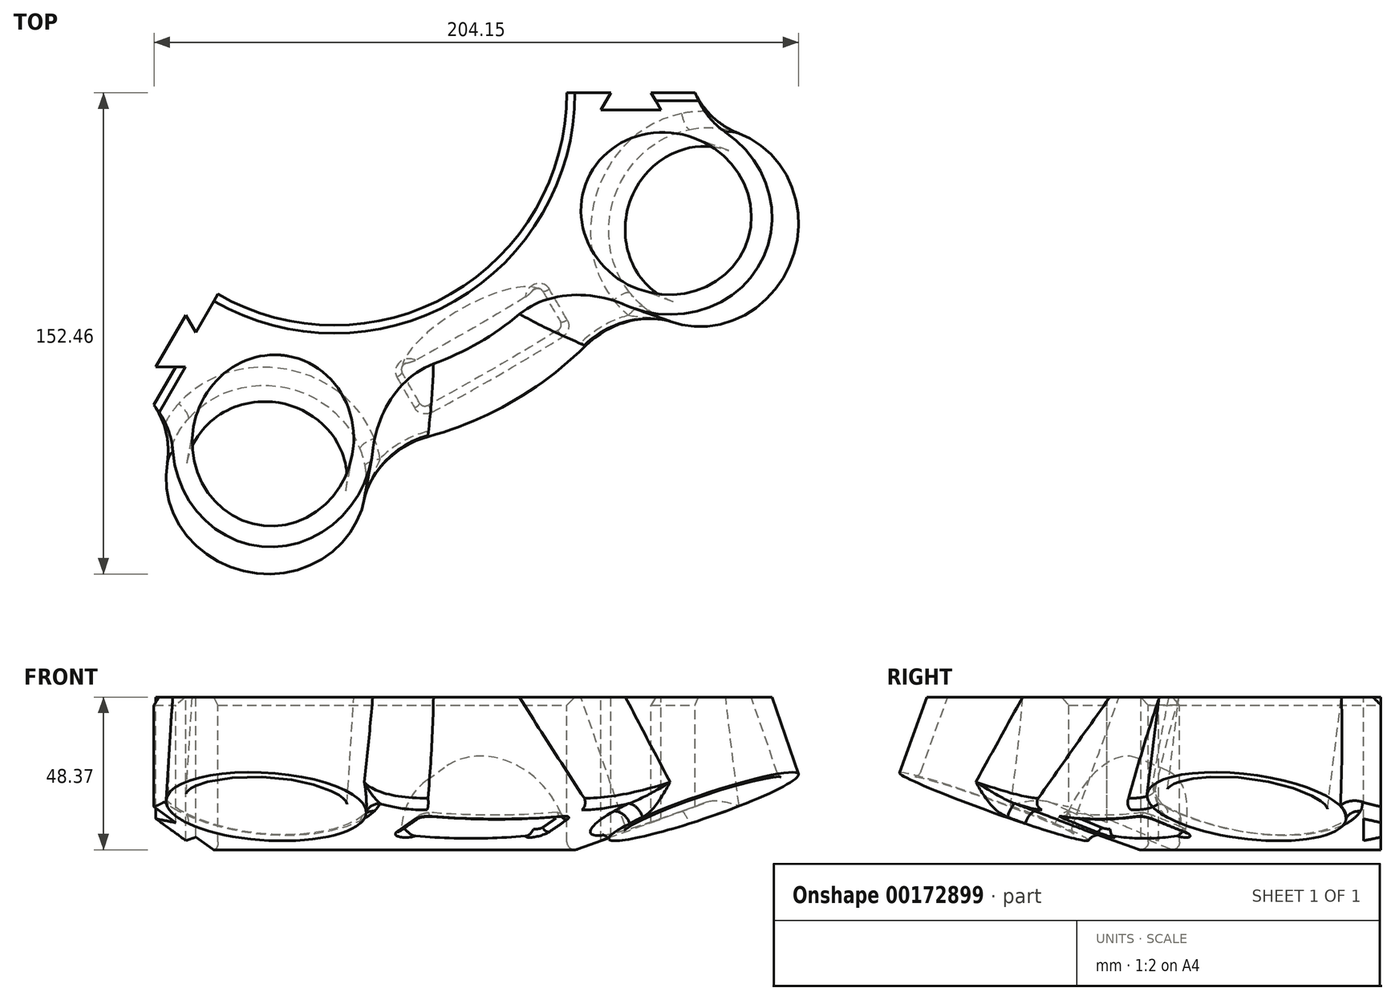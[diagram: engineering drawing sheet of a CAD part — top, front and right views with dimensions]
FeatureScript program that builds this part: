
annotation { "Feature Type Name" : "Feature", "Feature Type Description" : "" }
export const myFeature = defineFeature(function(context is Context, id is Id, definition is map)
    precondition{}
    {
        {
            var Q0;
            Q0=qCreatedBy(makeId("Top.planeOp"),FACE);
            var sketch = newSketch(context, id + "F0", { "sketchPlane" : qUnion([Q0])});
            skArc(sketch, "E0", {"start": v(36.2, 62.7) * mm, "mid": v(-36.2, 62.7) * mm, "end": v(-72.39, 0) * mm});
            skArc(sketch, "E1", {"start": v(55.44, 96.02) * mm, "mid": v(43.6, 101.94) * mm, "end": v(31.13, 106.41) * mm});
            skLineSegment(sketch, "E2", {"start": v(-72.4, 0) * mm, "end": v(-110.87, 0) * mm});
            skLineSegment(sketch, "E3", {"start": v(36.2, 62.7) * mm, "end": v(55.44, 96.02) * mm});
            skLineSegment(sketch, "E4", {"start": v(-22.63, 115.53) * mm, "end": v(0, 0) * mm, "construction": true});
            skLineSegment(sketch, "E5", {"start": v(-90.19, 75.67) * mm, "end": v(0, 0) * mm, "construction": true});
            skPoint(sketch, "E6.visualSharp", {"position": v(-104.04, 38.3) * mm});
            skPoint(sketch, "E7.visualSharp", {"position": v(-57.88, 98.1) * mm});
            skPoint(sketch, "E8.visualSharp", {"position": v(16.78, 109.6) * mm});
            skArc(sketch, "E9.converted", {"start": v(55.44, 96.02) * mm, "mid": v(-55.44, 96.02) * mm, "end": v(-110.87, 0) * mm});
            skSolve(sketch);
        }
        {
            var Q0;
            Q0=qCreatedBy(makeId("Front.planeOp"),FACE);
            var Q1;
            Q1=sQuery(id+"F0.wireOp",EDGE,"E5");
            cPlane(context, id + "F1", {"entities" : qUnion([Q0, Q1]), "cplaneType" : CPlaneType.LINE_ANGLE, "offset" : 25.4 * mm, "angle" : 0 * degree, "width" : 152.4 * mm, "height" : 152.4 * mm});
        }
        {
            var Q0;
            Q0=qCreatedBy(id+"F1.planeOp",FACE);
            var sketch = newSketch(context, id + "F2", { "sketchPlane" : qUnion([Q0])});
            skLineSegment(sketch, "E10", {"start": v(91.59, 0) * mm, "end": v(119.1, 10.02) * mm, "construction": true});
            skSolve(sketch);
        }
        {
            var Q0;
            Q0=qCreatedBy(id+"F1.planeOp",FACE);
            var Q1;
            Q1=sQuery(id+"F0.wireOp",EDGE,"E4");
            cPlane(context, id + "F3", {"entities" : qUnion([Q0, Q1]), "cplaneType" : CPlaneType.LINE_ANGLE, "offset" : 25.4 * mm, "angle" : 0 * degree, "width" : 152.4 * mm, "height" : 152.4 * mm});
        }
        {
            var Q0;
            Q0=qCreatedBy(id+"F3.planeOp",FACE);
            var sketch = newSketch(context, id + "F4", { "sketchPlane" : qUnion([Q0])});
            skLineSegment(sketch, "E11", {"start": v(-91.91, 0) * mm, "end": v(-139.27, 17.24) * mm, "construction": true});
            skSolve(sketch);
        }
        {
            var Q0;
            Q0=qCreatedBy(id+"F1.planeOp",FACE);
            var sketch = newSketch(context, id + "F5", { "sketchPlane" : qUnion([Q0])});
            skLineSegment(sketch, "E12", {"start": v(0, 0) * mm, "end": v(124.46, 0) * mm, "construction": true});
            skLineSegment(sketch, "E13", {"start": v(0, 53.66) * mm, "end": v(0, 0) * mm, "construction": true});
            skLineSegment(sketch, "E14", {"start": v(124.46, 0) * mm, "end": v(106, 50.72) * mm, "construction": true});
            skLineSegment(sketch, "E15", {"start": v(148.36, 8.7) * mm, "end": v(154.3, 10.86) * mm});
            skLineSegment(sketch, "E16", {"start": v(154.3, 10.86) * mm, "end": v(134.75, 64.56) * mm});
            skLineSegment(sketch, "E17", {"start": v(134.75, 64.56) * mm, "end": v(129.03, 61.8) * mm});
            skLineSegment(sketch, "E18", {"start": v(148.36, 8.7) * mm, "end": v(129.03, 61.8) * mm});
            skSolve(sketch);
        }
        {
            var Q0;
            Q0 = qSketchRegion(id + "F5", true);
            var Q1;
            Q1=sQuery(id+"F5.wireOp",EDGE,"E14");
            revolve(context, id + "F6", {"entities" : qUnion([Q0]), "axis" : qUnion([Q1]), "revolveType" : RevolveType.FULL});
        }
        {
            var Q0;
            Q0=makeQuery(id+"F6.opRevolve","SWEPT_BODY",BODY,{"disambiguationData":[OSD([sQuery(id+"F5.wireOp",EDGE,"E15"),sQuery(id+"F5.wireOp",EDGE,"E16"),sQuery(id+"F5.wireOp",EDGE,"E17"),sQuery(id+"F5.wireOp",EDGE,"E18")])]});
            var Q1;
            Q1=sQuery(id+"F5.wireOp",EDGE,"E13");
            circularPattern(context, id + "F7", {"entities" : qUnion([Q0]), "axis" : qUnion([Q1]), "angle" : 40 * degree, "instanceCount" : 2});
        }
        {
            var Q0;
            Q0=qCreatedBy(id+"F1.planeOp",FACE);
            var sketch = newSketch(context, id + "F8", { "sketchPlane" : qUnion([Q0])});
            skLineSegment(sketch, "E19", {"start": v(73.66, 34.68) * mm, "end": v(73.66, -14.78) * mm});
            skLineSegment(sketch, "E20", {"start": v(73.66, -14.78) * mm, "end": v(73.66, 34.68) * mm});
            skLineSegment(sketch, "E21", {"start": v(73.66, 34.68) * mm, "end": v(91.44, 34.68) * mm});
            skLineSegment(sketch, "E22", {"start": v(114.27, 0) * mm, "end": v(73.66, -14.78) * mm});
            skLineSegment(sketch, "E23", {"start": v(91.44, 34.68) * mm, "end": v(114.27, 0) * mm});
            skSolve(sketch);
        }
        {
            var Q0;
            Q0 = qSketchRegion(id + "F8", true);
            var Q1;
            Q1=sQuery(id+"F5.wireOp",EDGE,"E13");
            revolve(context, id + "F9", {"entities" : qUnion([Q0]), "axis" : qUnion([Q1]), "revolveType" : RevolveType.TWO_DIRECTIONS, "angle" : 80 * degree, "angleBack" : 320 * degree});
        }
        {
            var Q0;
            Q0=makeQuery(id+"F6.opRevolve","SWEPT_FACE",FACE,{"disambiguationData":[OSD([sQuery(id+"F5.wireOp",EDGE,"E15")])]});
            var sketch = newSketch(context, id + "F10", { "sketchPlane" : qUnion([Q0])});
            skCircle(sketch, "E24", {"center": v(-87.24, -77.9) * mm, "radius": 25.53 * mm});
            skSolve(sketch);
        }
        {
            var Q0;
            Q0 = qSketchRegion(id + "F10", true);
            extrude(context, id + "F11", {"entities" : qUnion([Q0]), "operationType" : NewBodyOperationType.REMOVE, "endBound" : BoundingType.THROUGH_ALL, "depth" : 25.4 * mm, "hasSecondDirection" : true, "secondDirectionBound" : BoundingType.THROUGH_ALL, "secondDirectionOppositeDirection" : true, "secondDirectionDepth" : 25.4 * mm});
        }
        {
            var Q0;
            Q0=makeQuery(id+"F7.opPattern","COPY",FACE,{"derivedFrom":makeQuery(id+"F6.opRevolve","SWEPT_FACE",FACE,{"disambiguationData":[OSD([sQuery(id+"F5.wireOp",EDGE,"E15")])]}),"instanceName":"1"});
            var sketch = newSketch(context, id + "F12", { "sketchPlane" : qUnion([Q0])});
            skCircle(sketch, "E25", {"center": v(-19.12, -115.38) * mm, "radius": 25.53 * mm});
            skSolve(sketch);
        }
        {
            var Q0;
            Q0 = qSketchRegion(id + "F12", true);
            extrude(context, id + "F13", {"entities" : qUnion([Q0]), "operationType" : NewBodyOperationType.REMOVE, "endBound" : BoundingType.THROUGH_ALL, "depth" : 25.4 * mm, "hasSecondDirection" : true, "secondDirectionBound" : BoundingType.THROUGH_ALL, "secondDirectionOppositeDirection" : true, "secondDirectionDepth" : 25.4 * mm});
        }
        {
            var Q0;
            Q0=makeQuery(id+"F9.opRevolve","CAP_FACE",FACE,{"disambiguationData":[OSD([sQuery(id+"F8.wireOp",EDGE,"E19"),sQuery(id+"F8.wireOp",EDGE,"E20"),sQuery(id+"F8.wireOp",EDGE,"E21"),sQuery(id+"F8.wireOp",EDGE,"E22"),sQuery(id+"F8.wireOp",EDGE,"E23")])],"isStart":true});
            var sketch = newSketch(context, id + "F14", { "sketchPlane" : qUnion([Q0])});
            skLineSegment(sketch, "E26", {"start": v(-73.66, 34.68) * mm, "end": v(-150.81, 34.68) * mm});
            skLineSegment(sketch, "E27", {"start": v(-150.81, 69.54) * mm, "end": v(-73.66, 69.54) * mm});
            skLineSegment(sketch, "E28", {"start": v(-150.81, 69.54) * mm, "end": v(-150.81, 34.68) * mm});
            skLineSegment(sketch, "E29", {"start": v(-73.66, 69.54) * mm, "end": v(-73.66, 34.68) * mm});
            skSolve(sketch);
        }
        {
            var Q0;
            Q0 = qSketchRegion(id + "F14", true);
            var Q1;
            Q1=sQuery(id+"F5.wireOp",EDGE,"E13");
            revolve(context, id + "F15", {"operationType" : NewBodyOperationType.REMOVE, "entities" : qUnion([Q0]), "axis" : qUnion([Q1]), "revolveType" : RevolveType.ONE_DIRECTION, "angle" : 120 * degree});
        }
        {
            var Q0;
            Q0=makeQuery(id+"F6.opRevolve","SWEPT_BODY",BODY,{"disambiguationData":[OSD([sQuery(id+"F5.wireOp",EDGE,"E15"),sQuery(id+"F5.wireOp",EDGE,"E16"),sQuery(id+"F5.wireOp",EDGE,"E17"),sQuery(id+"F5.wireOp",EDGE,"E18")])]});
            var Q1;
            Q1=makeQuery(id+"F7.opPattern","COPY",BODY,{"derivedFrom":makeQuery(id+"F6.opRevolve","SWEPT_BODY",BODY,{"disambiguationData":[OSD([sQuery(id+"F5.wireOp",EDGE,"E15"),sQuery(id+"F5.wireOp",EDGE,"E16"),sQuery(id+"F5.wireOp",EDGE,"E17"),sQuery(id+"F5.wireOp",EDGE,"E18")])]}),"instanceName":"1"});
            var Q2;
            Q2=makeQuery(id+"F9.opRevolve","SWEPT_BODY",BODY,{"disambiguationData":[OSD([sQuery(id+"F8.wireOp",EDGE,"E19"),sQuery(id+"F8.wireOp",EDGE,"E20"),sQuery(id+"F8.wireOp",EDGE,"E21"),sQuery(id+"F8.wireOp",EDGE,"E22"),sQuery(id+"F8.wireOp",EDGE,"E23")])]});
            var Q3;
            Q3=sQuery(id+"F5.wireOp",EDGE,"E13");
            circularPattern(context, id + "F16", {"entities" : qUnion([Q0, Q1, Q2]), "axis" : qUnion([Q3]), "angle" : 120 * degree, "instanceCount" : 3});
        }
        {
            var Q0;
            Q0=qCreatedBy(makeId("Front.planeOp"),FACE);
            var sketch = newSketch(context, id + "F17", { "sketchPlane" : qUnion([Q0])});
            skLineSegment(sketch, "E30", {"start": v(-105.19, -47.93) * mm, "end": v(-151.02, -47.93) * mm, "construction": true});
            skLineSegment(sketch, "E31", {"start": v(-102.98, -8.48) * mm, "end": v(-100.37, -1.32) * mm});
            skLineSegment(sketch, "E32", {"start": v(-102.98, -8.48) * mm, "end": v(-129.23, 1.07) * mm});
            skLineSegment(sketch, "E33", {"start": v(-129.23, 1.07) * mm, "end": v(-126.63, 8.23) * mm});
            skLineSegment(sketch, "E34", {"start": v(-126.63, 8.23) * mm, "end": v(-100.37, -1.32) * mm});
            skLineSegment(sketch, "E35", {"start": v(-135.33, -8.25) * mm, "end": v(-127.68, 12.78) * mm, "construction": true});
            skSolve(sketch);
        }
        {
            var Q0;
            Q0=makeQuery(id+"FokKAQGzDr6NISq_2.opRevolve","SWEPT_BODY",BODY,{"disambiguationData":[OSD([sQuery(id+"F17.wireOp",EDGE,"E31"),sQuery(id+"F17.wireOp",EDGE,"E32"),sQuery(id+"F17.wireOp",EDGE,"E33"),sQuery(id+"F17.wireOp",EDGE,"E34")])]});
            var Q1;
            Q1=makeQuery(id+"F9.opRevolve","SWEPT_BODY",BODY,{"disambiguationData":[OSD([sQuery(id+"F8.wireOp",EDGE,"E19"),sQuery(id+"F8.wireOp",EDGE,"E20"),sQuery(id+"F8.wireOp",EDGE,"E21"),sQuery(id+"F8.wireOp",EDGE,"E22"),sQuery(id+"F8.wireOp",EDGE,"E23")])]});
            var Q2;
            Q2=sQuery(id+"F5.wireOp",EDGE,"E13");
            circularPattern(context, id + "F18", {"entities" : qUnion([Q0, Q1]), "axis" : qUnion([Q2]), "angle" : 120 * degree, "instanceCount" : 3});
        }
        {
            var Q0;
            {var subQ0=sQuery(id+"F8.wireOp",EDGE,"E22");var subQ2=sQuery(id+"F8.wireOp",EDGE,"E23");var subQ4=sQuery(id+"F8.wireOp",EDGE,"E21");var subQ5=makeQuery(id+"F11.opExtrude","SWEPT_FACE",FACE,{"disambiguationData":[OSD([sQuery(id+"F10.wireOp",EDGE,"E24")])]});Q0=makeQuery(id+"F16.opPattern","COPY",EDGE,{"derivedFrom":makeQuery(id+"F13.boolean.opBoolean","SPLIT",EDGE,{"disambiguationData":[TD([makeQuery(id+"F11.boolean.opBoolean","COPY",FACE,{"disambiguationData":[TD([makeQuery(id+"F9.opRevolve","SWEPT_FACE",FACE,{"disambiguationData":[OSD([subQ4])]})])],"derivedFrom":subQ5})])],"derivedFrom":makeQuery(id+"F11.boolean.opBoolean","SPLIT",EDGE,{"disambiguationData":[TD([makeQuery(id+"F9.opRevolve","CAP_FACE",FACE,{"disambiguationData":[OSD([sQuery(id+"F8.wireOp",EDGE,"E19"),sQuery(id+"F8.wireOp",EDGE,"E20"),subQ4,subQ0,subQ2])],"isStart":false})])],"derivedFrom":makeQuery(id+"F9.opRevolve","SWEPT_EDGE",EDGE,{"disambiguationData":[OSD([subQ0,subQ2])]})})}),"instanceName":"1"});}
            fillet(context, id + "F19", {"entities" : qUnion([Q0]), "radius" : 5.08 * mm, "tangentPropagation" : true, "allowEdgeOverflow" : false});
        }
        {
            var Q0;
            Q0=makeQuery(id+"F18.opPattern","COPY",BODY,{"derivedFrom":makeQuery(id+"FokKAQGzDr6NISq_2.opRevolve","SWEPT_BODY",BODY,{"disambiguationData":[OSD([sQuery(id+"F17.wireOp",EDGE,"E31"),sQuery(id+"F17.wireOp",EDGE,"E32"),sQuery(id+"F17.wireOp",EDGE,"E33"),sQuery(id+"F17.wireOp",EDGE,"E34")])]}),"instanceName":"1"});
            var Q1;
            Q1=makeQuery(id+"F6.opRevolve","SWEPT_BODY",BODY,{"disambiguationData":[OSD([sQuery(id+"F5.wireOp",EDGE,"E15"),sQuery(id+"F5.wireOp",EDGE,"E16"),sQuery(id+"F5.wireOp",EDGE,"E17"),sQuery(id+"F5.wireOp",EDGE,"E18")])]});
            var Q2;
            Q2=makeQuery(id+"F16.opPattern","COPY",BODY,{"derivedFrom":makeQuery(id+"F9.opRevolve","SWEPT_BODY",BODY,{"disambiguationData":[OSD([sQuery(id+"F8.wireOp",EDGE,"E19"),sQuery(id+"F8.wireOp",EDGE,"E20"),sQuery(id+"F8.wireOp",EDGE,"E21"),sQuery(id+"F8.wireOp",EDGE,"E22"),sQuery(id+"F8.wireOp",EDGE,"E23")])]}),"instanceName":"1"});
            var Q3;
            Q3=makeQuery(id+"F18.opPattern","COPY",BODY,{"derivedFrom":makeQuery(id+"F9.opRevolve","SWEPT_BODY",BODY,{"disambiguationData":[OSD([sQuery(id+"F8.wireOp",EDGE,"E19"),sQuery(id+"F8.wireOp",EDGE,"E20"),sQuery(id+"F8.wireOp",EDGE,"E21"),sQuery(id+"F8.wireOp",EDGE,"E22"),sQuery(id+"F8.wireOp",EDGE,"E23")])]}),"instanceName":"1"});
            var Q4;
            Q4=makeQuery(id+"F18.opPattern","COPY",BODY,{"derivedFrom":makeQuery(id+"F9.opRevolve","SWEPT_BODY",BODY,{"disambiguationData":[OSD([sQuery(id+"F8.wireOp",EDGE,"E19"),sQuery(id+"F8.wireOp",EDGE,"E20"),sQuery(id+"F8.wireOp",EDGE,"E21"),sQuery(id+"F8.wireOp",EDGE,"E22"),sQuery(id+"F8.wireOp",EDGE,"E23")])]}),"instanceName":"2"});
            var Q5;
            Q5=makeQuery(id+"F7.opPattern","COPY",BODY,{"derivedFrom":makeQuery(id+"F6.opRevolve","SWEPT_BODY",BODY,{"disambiguationData":[OSD([sQuery(id+"F5.wireOp",EDGE,"E15"),sQuery(id+"F5.wireOp",EDGE,"E16"),sQuery(id+"F5.wireOp",EDGE,"E17"),sQuery(id+"F5.wireOp",EDGE,"E18")])]}),"instanceName":"1"});
            var Q6;
            Q6=makeQuery(id+"F16.opPattern","COPY",BODY,{"derivedFrom":makeQuery(id+"F6.opRevolve","SWEPT_BODY",BODY,{"disambiguationData":[OSD([sQuery(id+"F5.wireOp",EDGE,"E15"),sQuery(id+"F5.wireOp",EDGE,"E16"),sQuery(id+"F5.wireOp",EDGE,"E17"),sQuery(id+"F5.wireOp",EDGE,"E18")])]}),"instanceName":"1"});
            var Q7;
            Q7=makeQuery(id+"FokKAQGzDr6NISq_2.opRevolve","SWEPT_BODY",BODY,{"disambiguationData":[OSD([sQuery(id+"F17.wireOp",EDGE,"E31"),sQuery(id+"F17.wireOp",EDGE,"E32"),sQuery(id+"F17.wireOp",EDGE,"E33"),sQuery(id+"F17.wireOp",EDGE,"E34")])]});
            var Q8;
            Q8=makeQuery(id+"F16.opPattern","COPY",BODY,{"derivedFrom":makeQuery(id+"F9.opRevolve","SWEPT_BODY",BODY,{"disambiguationData":[OSD([sQuery(id+"F8.wireOp",EDGE,"E19"),sQuery(id+"F8.wireOp",EDGE,"E20"),sQuery(id+"F8.wireOp",EDGE,"E21"),sQuery(id+"F8.wireOp",EDGE,"E22"),sQuery(id+"F8.wireOp",EDGE,"E23")])]}),"instanceName":"2"});
            var Q9;
            Q9=makeQuery(id+"F16.opPattern","COPY",BODY,{"derivedFrom":makeQuery(id+"F7.opPattern","COPY",BODY,{"derivedFrom":makeQuery(id+"F6.opRevolve","SWEPT_BODY",BODY,{"disambiguationData":[OSD([sQuery(id+"F5.wireOp",EDGE,"E15"),sQuery(id+"F5.wireOp",EDGE,"E16"),sQuery(id+"F5.wireOp",EDGE,"E17"),sQuery(id+"F5.wireOp",EDGE,"E18")])]}),"instanceName":"1"}),"instanceName":"2"});
            var Q10;
            Q10=makeQuery(id+"F18.opPattern","COPY",BODY,{"derivedFrom":makeQuery(id+"FokKAQGzDr6NISq_2.opRevolve","SWEPT_BODY",BODY,{"disambiguationData":[OSD([sQuery(id+"F17.wireOp",EDGE,"E31"),sQuery(id+"F17.wireOp",EDGE,"E32"),sQuery(id+"F17.wireOp",EDGE,"E33"),sQuery(id+"F17.wireOp",EDGE,"E34")])]}),"instanceName":"2"});
            var Q11;
            Q11=makeQuery(id+"F16.opPattern","COPY",BODY,{"derivedFrom":makeQuery(id+"F7.opPattern","COPY",BODY,{"derivedFrom":makeQuery(id+"F6.opRevolve","SWEPT_BODY",BODY,{"disambiguationData":[OSD([sQuery(id+"F5.wireOp",EDGE,"E15"),sQuery(id+"F5.wireOp",EDGE,"E16"),sQuery(id+"F5.wireOp",EDGE,"E17"),sQuery(id+"F5.wireOp",EDGE,"E18")])]}),"instanceName":"1"}),"instanceName":"1"});
            var Q12;
            Q12=makeQuery(id+"F16.opPattern","COPY",BODY,{"derivedFrom":makeQuery(id+"F6.opRevolve","SWEPT_BODY",BODY,{"disambiguationData":[OSD([sQuery(id+"F5.wireOp",EDGE,"E15"),sQuery(id+"F5.wireOp",EDGE,"E16"),sQuery(id+"F5.wireOp",EDGE,"E17"),sQuery(id+"F5.wireOp",EDGE,"E18")])]}),"instanceName":"2"});
            var Q13;
            Q13=makeQuery(id+"F9.opRevolve","SWEPT_BODY",BODY,{"disambiguationData":[OSD([sQuery(id+"F8.wireOp",EDGE,"E19"),sQuery(id+"F8.wireOp",EDGE,"E20"),sQuery(id+"F8.wireOp",EDGE,"E21"),sQuery(id+"F8.wireOp",EDGE,"E22"),sQuery(id+"F8.wireOp",EDGE,"E23")])]});
            booleanBodies(context, id + "F20", {"operationType" : BooleanOperationType.UNION, "tools" : qUnion([Q0, Q1, Q2, Q3, Q4, Q5, Q6, Q7, Q8, Q9, Q10, Q11, Q12, Q13])});
        }
        {
            var Q0;
            {var subQ0=sQuery(id+"F8.wireOp",EDGE,"E23");var subQ1=sQuery(id+"F8.wireOp",EDGE,"E22");var subQ2=sQuery(id+"F8.wireOp",EDGE,"E21");var subQ3=sQuery(id+"F8.wireOp",EDGE,"E20");var subQ4=sQuery(id+"F8.wireOp",EDGE,"E19");var subQ8=makeQuery(id+"F9.opRevolve","SWEPT_FACE",FACE,{"disambiguationData":[OSD([subQ0])]});var subQ9=makeQuery(id+"F11.boolean.opBoolean","SPLIT",FACE,{"disambiguationData":[TD([makeQuery(id+"F9.opRevolve","CAP_FACE",FACE,{"disambiguationData":[OSD([subQ4,subQ3,subQ2,subQ1,subQ0])],"isStart":true})])],"derivedFrom":subQ8});var subQ10=makeQuery(id+"F9.opRevolve","CAP_FACE",FACE,{"disambiguationData":[OSD([subQ4,subQ3,subQ2,subQ1,subQ0])],"isStart":false});Q0=makeQuery(id+"F20.opBoolean","INTERSECT",EDGE,{"derivedFrom":[makeQuery(id+"F13.boolean.opBoolean","SPLIT",FACE,{"disambiguationData":[TD([subQ10])],"derivedFrom":makeQuery(id+"F11.boolean.opBoolean","SPLIT",FACE,{"disambiguationData":[TD([subQ10])],"derivedFrom":subQ8})}),makeQuery(id+"F16.opPattern","COPY",FACE,{"derivedFrom":subQ9,"instanceName":"1"}),makeQuery(id+"F16.opPattern","COPY",FACE,{"derivedFrom":makeQuery(id+"F6.opRevolve","SWEPT_FACE",FACE,{"disambiguationData":[OSD([sQuery(id+"F5.wireOp",EDGE,"E16")])]}),"instanceName":"1"}),makeQuery(id+"F18.opPattern","COPY",FACE,{"derivedFrom":subQ9,"instanceName":"1"})]});}
            var Q1;
            {var subQ0=sQuery(id+"F8.wireOp",EDGE,"E23");var subQ1=sQuery(id+"F8.wireOp",EDGE,"E22");var subQ2=sQuery(id+"F8.wireOp",EDGE,"E21");Q1=makeQuery(id+"F20.opBoolean","INTERSECT",EDGE,{"derivedFrom":[makeQuery(id+"F11.boolean.opBoolean","SPLIT",FACE,{"disambiguationData":[TD([makeQuery(id+"F9.opRevolve","CAP_FACE",FACE,{"disambiguationData":[OSD([sQuery(id+"F8.wireOp",EDGE,"E19"),sQuery(id+"F8.wireOp",EDGE,"E20"),subQ2,subQ1,subQ0])],"isStart":true})])],"derivedFrom":makeQuery(id+"F9.opRevolve","SWEPT_FACE",FACE,{"disambiguationData":[OSD([subQ0])]})}),makeQuery(id+"F6.opRevolve","SWEPT_FACE",FACE,{"disambiguationData":[OSD([sQuery(id+"F5.wireOp",EDGE,"E16")])]})]});}
            var Q2;
            {var subQ0=sQuery(id+"F8.wireOp",EDGE,"E23");var subQ1=sQuery(id+"F8.wireOp",EDGE,"E22");var subQ2=sQuery(id+"F8.wireOp",EDGE,"E21");var subQ3=sQuery(id+"F8.wireOp",EDGE,"E20");var subQ4=sQuery(id+"F8.wireOp",EDGE,"E19");var subQ5=makeQuery(id+"F9.opRevolve","CAP_FACE",FACE,{"disambiguationData":[OSD([subQ4,subQ3,subQ2,subQ1,subQ0])],"isStart":false});var subQ9=makeQuery(id+"F9.opRevolve","SWEPT_FACE",FACE,{"disambiguationData":[OSD([subQ0])]});var subQ10=makeQuery(id+"F13.boolean.opBoolean","SPLIT",FACE,{"disambiguationData":[TD([subQ5])],"derivedFrom":makeQuery(id+"F11.boolean.opBoolean","SPLIT",FACE,{"disambiguationData":[TD([subQ5])],"derivedFrom":subQ9})});Q2=makeQuery(id+"F20.opBoolean","INTERSECT",EDGE,{"derivedFrom":[makeQuery(id+"F11.boolean.opBoolean","SPLIT",FACE,{"disambiguationData":[TD([makeQuery(id+"F9.opRevolve","CAP_FACE",FACE,{"disambiguationData":[OSD([subQ4,subQ3,subQ2,subQ1,subQ0])],"isStart":true})])],"derivedFrom":subQ9}),makeQuery(id+"F16.opPattern","COPY",FACE,{"derivedFrom":subQ10,"instanceName":"2"}),makeQuery(id+"F16.opPattern","COPY",FACE,{"derivedFrom":makeQuery(id+"F7.opPattern","COPY",FACE,{"derivedFrom":makeQuery(id+"F6.opRevolve","SWEPT_FACE",FACE,{"disambiguationData":[OSD([sQuery(id+"F5.wireOp",EDGE,"E16")])]}),"instanceName":"1"}),"instanceName":"2"}),makeQuery(id+"F18.opPattern","COPY",FACE,{"derivedFrom":subQ10,"instanceName":"2"})]});}
            var Q3;
            {var subQ0=sQuery(id+"F8.wireOp",EDGE,"E23");var subQ1=sQuery(id+"F8.wireOp",EDGE,"E22");var subQ2=sQuery(id+"F8.wireOp",EDGE,"E21");var subQ3=makeQuery(id+"F11.boolean.opBoolean","SPLIT",FACE,{"disambiguationData":[TD([makeQuery(id+"F9.opRevolve","CAP_FACE",FACE,{"disambiguationData":[OSD([sQuery(id+"F8.wireOp",EDGE,"E19"),sQuery(id+"F8.wireOp",EDGE,"E20"),subQ2,subQ1,subQ0])],"isStart":true})])],"derivedFrom":makeQuery(id+"F9.opRevolve","SWEPT_FACE",FACE,{"disambiguationData":[OSD([subQ0])]})});Q3=makeQuery(id+"F20.opBoolean","INTERSECT",EDGE,{"derivedFrom":[makeQuery(id+"F16.opPattern","COPY",FACE,{"derivedFrom":subQ3,"instanceName":"2"}),makeQuery(id+"F16.opPattern","COPY",FACE,{"derivedFrom":makeQuery(id+"F6.opRevolve","SWEPT_FACE",FACE,{"disambiguationData":[OSD([sQuery(id+"F5.wireOp",EDGE,"E16")])]}),"instanceName":"2"}),makeQuery(id+"F18.opPattern","COPY",FACE,{"derivedFrom":subQ3,"instanceName":"2"})]});}
            var Q4;
            {var subQ0=sQuery(id+"F8.wireOp",EDGE,"E23");var subQ1=sQuery(id+"F8.wireOp",EDGE,"E22");var subQ2=sQuery(id+"F8.wireOp",EDGE,"E21");var subQ3=sQuery(id+"F8.wireOp",EDGE,"E20");var subQ4=sQuery(id+"F8.wireOp",EDGE,"E19");var subQ8=makeQuery(id+"F9.opRevolve","SWEPT_FACE",FACE,{"disambiguationData":[OSD([subQ0])]});var subQ9=makeQuery(id+"F9.opRevolve","CAP_FACE",FACE,{"disambiguationData":[OSD([subQ4,subQ3,subQ2,subQ1,subQ0])],"isStart":false});var subQ10=makeQuery(id+"F13.boolean.opBoolean","SPLIT",FACE,{"disambiguationData":[TD([subQ9])],"derivedFrom":makeQuery(id+"F11.boolean.opBoolean","SPLIT",FACE,{"disambiguationData":[TD([subQ9])],"derivedFrom":subQ8})});Q4=makeQuery(id+"F20.opBoolean","INTERSECT",EDGE,{"derivedFrom":[makeQuery(id+"F16.opPattern","COPY",FACE,{"derivedFrom":subQ10,"instanceName":"1"}),makeQuery(id+"F16.opPattern","COPY",FACE,{"derivedFrom":makeQuery(id+"F7.opPattern","COPY",FACE,{"derivedFrom":makeQuery(id+"F6.opRevolve","SWEPT_FACE",FACE,{"disambiguationData":[OSD([sQuery(id+"F5.wireOp",EDGE,"E16")])]}),"instanceName":"1"}),"instanceName":"1"}),makeQuery(id+"F18.opPattern","COPY",FACE,{"derivedFrom":subQ10,"instanceName":"1"}),makeQuery(id+"F18.opPattern","COPY",FACE,{"derivedFrom":makeQuery(id+"F11.boolean.opBoolean","SPLIT",FACE,{"disambiguationData":[TD([makeQuery(id+"F9.opRevolve","CAP_FACE",FACE,{"disambiguationData":[OSD([subQ4,subQ3,subQ2,subQ1,subQ0])],"isStart":true})])],"derivedFrom":subQ8}),"instanceName":"2"})]});}
            var Q5;
            {var subQ0=sQuery(id+"F8.wireOp",EDGE,"E23");var subQ1=sQuery(id+"F8.wireOp",EDGE,"E22");var subQ2=sQuery(id+"F8.wireOp",EDGE,"E21");var subQ3=makeQuery(id+"F9.opRevolve","CAP_FACE",FACE,{"disambiguationData":[OSD([sQuery(id+"F8.wireOp",EDGE,"E19"),sQuery(id+"F8.wireOp",EDGE,"E20"),subQ2,subQ1,subQ0])],"isStart":false});Q5=makeQuery(id+"F20.opBoolean","INTERSECT",EDGE,{"derivedFrom":[makeQuery(id+"F13.boolean.opBoolean","SPLIT",FACE,{"disambiguationData":[TD([subQ3])],"derivedFrom":makeQuery(id+"F11.boolean.opBoolean","SPLIT",FACE,{"disambiguationData":[TD([subQ3])],"derivedFrom":makeQuery(id+"F9.opRevolve","SWEPT_FACE",FACE,{"disambiguationData":[OSD([subQ0])]})})}),makeQuery(id+"F7.opPattern","COPY",FACE,{"derivedFrom":makeQuery(id+"F6.opRevolve","SWEPT_FACE",FACE,{"disambiguationData":[OSD([sQuery(id+"F5.wireOp",EDGE,"E16")])]}),"instanceName":"1"})]});}
            fillet(context, id + "F21", {"entities" : qUnion([Q0, Q1, Q2, Q3, Q4, Q5]), "radius" : 25.4 * mm, "tangentPropagation" : true, "allowEdgeOverflow" : false});
        }
        {
            var Q0;
            Q0=qCreatedBy(makeId("Right.planeOp"),FACE);
            var Q1;
            Q1=sQuery(id+"F17.wireOp",EDGE,"E31");
            cPlane(context, id + "F22", {"entities" : qUnion([Q0, Q1]), "cplaneType" : CPlaneType.LINE_ANGLE, "offset" : 25.4 * mm, "angle" : 0 * degree, "width" : 152.4 * mm, "height" : 152.4 * mm});
        }
        {
            var Q0;
            Q0=qCreatedBy(id+"F22.planeOp",FACE);
            var sketch = newSketch(context, id + "F23", { "sketchPlane" : qUnion([Q0])});
            skCircle(sketch, "E36", {"center": v(0, -43.2) * mm, "radius": 26.67 * mm});
            skSolve(sketch);
        }
        {
            var Q0;
            Q0 = qSketchRegion(id + "F23", true);
            extrude(context, id + "F24", {"entities" : qUnion([Q0]), "oppositeDirection" : true, "depth" : 16 * mm});
        }
        {
            var Q0;
            Q0=makeQuery(id+"F24.opExtrude","SWEPT_BODY",BODY,{"disambiguationData":[OSD([sQuery(id+"F23.wireOp",EDGE,"E36")])]});
            var Q1;
            Q1=sQuery(id+"F5.wireOp",EDGE,"E13");
            circularPattern(context, id + "F25", {"operationType" : NewBodyOperationType.REMOVE, "entities" : qUnion([Q0]), "axis" : qUnion([Q1]), "angle" : 120 * degree, "instanceCount" : 3});
        }
        {
            var Q0;
            Q0=qCreatedBy(makeId("Top.planeOp"),FACE);
            var sketch = newSketch(context, id + "F26", { "sketchPlane" : qUnion([Q0])});
            skLineSegment(sketch, "E37", {"start": v(0, 0) * mm, "end": v(193.48, 0) * mm});
            skLineSegment(sketch, "E38", {"start": v(0, 0) * mm, "end": v(-96.74, -167.56) * mm});
            skArc(sketch, "E39", {"start": v(193.48, 0) * mm, "mid": v(-96.74, 167.56) * mm, "end": v(-96.74, -167.56) * mm});
            skSolve(sketch);
        }
        {
            var Q0;
            Q0 = qSketchRegion(id + "F26", true);
            extrude(context, id + "F27", {"entities" : qUnion([Q0]), "operationType" : NewBodyOperationType.REMOVE, "endBound" : BoundingType.THROUGH_ALL, "oppositeDirection" : true, "depth" : 25.4 * mm, "hasSecondDirection" : true, "secondDirectionBound" : BoundingType.THROUGH_ALL, "secondDirectionOppositeDirection" : false, "secondDirectionDepth" : 25.4 * mm});
        }
        {
            var Q0;
            {var subQ0=makeQuery(id+"F9.opRevolve","SWEPT_FACE",FACE,{"disambiguationData":[OSD([sQuery(id+"F8.wireOp",EDGE,"E21")])]});var subQ1=makeQuery(id+"F6.opRevolve","SWEPT_FACE",FACE,{"disambiguationData":[OSD([sQuery(id+"F5.wireOp",EDGE,"E16")])]});var subQ4=makeQuery(id+"F15.opRevolve","SWEPT_FACE",FACE,{"disambiguationData":[OSD([sQuery(id+"F14.wireOp",EDGE,"E26")])]});var subQ5=makeQuery(id+"F15.boolean.opBoolean","COPY",FACE,{"disambiguationData":[TD([makeQuery(id+"F7.opPattern","COPY",FACE,{"derivedFrom":subQ1,"instanceName":"1"})])],"derivedFrom":subQ4});var subQ6=makeQuery(id+"F15.boolean.opBoolean","COPY",FACE,{"disambiguationData":[TD([subQ1])],"derivedFrom":subQ4});Q0=makeQuery(id+"F34.boolean.opBoolean","MERGE",FACE,{"derivedFrom":[makeQuery(id+"F20.opBoolean","MERGE",FACE,{"derivedFrom":[subQ0,subQ6,subQ5,makeQuery(id+"F16.opPattern","COPY",FACE,{"derivedFrom":subQ0,"instanceName":"1"}),makeQuery(id+"F16.opPattern","COPY",FACE,{"derivedFrom":subQ6,"instanceName":"1"}),makeQuery(id+"F16.opPattern","COPY",FACE,{"derivedFrom":subQ5,"instanceName":"1"}),makeQuery(id+"F16.opPattern","COPY",FACE,{"derivedFrom":subQ0,"instanceName":"2"}),makeQuery(id+"F16.opPattern","COPY",FACE,{"derivedFrom":subQ6,"instanceName":"2"}),makeQuery(id+"F16.opPattern","COPY",FACE,{"derivedFrom":subQ5,"instanceName":"2"}),makeQuery(id+"F18.opPattern","COPY",FACE,{"derivedFrom":subQ0,"instanceName":"1"}),makeQuery(id+"F18.opPattern","COPY",FACE,{"derivedFrom":subQ0,"instanceName":"2"})]}),makeQuery(id+"F34.opExtrude","CAP_FACE",FACE,{"disambiguationData":[OSD([sQuery(id+"F33.wireOp",EDGE,"E51"),sQuery(id+"F33.wireOp",EDGE,"E52"),sQuery(id+"F33.wireOp",EDGE,"E53"),sQuery(id+"F33.wireOp",EDGE,"E54")])],"isStart":true})]});}
            var sketch = newSketch(context, id + "F28", { "sketchPlane" : qUnion([Q0])});
            skLineSegment(sketch, "E40", {"start": v(87.63, 0) * mm, "end": v(100.33, 0) * mm});
            skLineSegment(sketch, "E41", {"start": v(73.66, 0) * mm, "end": v(73.66, -14.95) * mm, "construction": true});
            skLineSegment(sketch, "E42", {"start": v(87.63, 0) * mm, "end": v(84.45, -5.5) * mm});
            skLineSegment(sketch, "E43", {"start": v(84.45, -5.5) * mm, "end": v(103.5, -5.5) * mm});
            skLineSegment(sketch, "E44", {"start": v(103.5, -5.5) * mm, "end": v(100.33, 0) * mm});
            skSolve(sketch);
        }
        {
            var Q0;
            {var subQ12=sQuery(id+"F33.wireOp",EDGE,"E53");Q0=makeQuery(id+"F34.boolean.opBoolean","SPLIT",FACE,{"disambiguationData":[TD([makeQuery(id+"F34.opExtrude","SWEPT_FACE",FACE,{"disambiguationData":[OSD([subQ12])]})])],"derivedFrom":makeQuery(id+"F27.boolean.opBoolean","COPY",FACE,{"derivedFrom":makeQuery(id+"F27.opExtrude","SWEPT_FACE",FACE,{"disambiguationData":[OSD([sQuery(id+"F26.wireOp",EDGE,"E38")])]})})});}
            var sketch = newSketch(context, id + "F29", { "sketchPlane" : qUnion([Q0])});
            skLineSegment(sketch, "E45", {"start": v(114.27, 0) * mm, "end": v(91.44, 34.68) * mm});
            skLineSegment(sketch, "E46", {"start": v(91.44, 34.68) * mm, "end": v(114.27, 34.68) * mm});
            skLineSegment(sketch, "E47", {"start": v(114.27, 34.68) * mm, "end": v(114.27, 0) * mm});
            skSolve(sketch);
        }
        {
            var Q0;
            Q0=makeQuery(id+"F29.imprint","IMPRINT",FACE,{"disambiguationData":[TD([[makeQuery(id+"F29.imprint","IMPRINT",EDGE,{"derivedFrom":sQuery(id+"F29.wireOp",EDGE,"E45")}),1.0]])]});
            var Q1;
            Q1 = qConstructionFilter(qBodyType(qCreatedBy(id + "F29" ,EDGE), BodyType.WIRE), ConstructionObject.NO);
            var Q2;
            Q2=sQuery(id+"F5.wireOp",EDGE,"E13");
            revolve(context, id + "F30", {"operationType" : NewBodyOperationType.ADD, "entities" : qUnion([Q0]), "surfaceEntities" : qUnion([Q1]), "axis" : qUnion([Q2]), "revolveType" : RevolveType.ONE_DIRECTION, "oppositeDirection" : true, "angle" : 6 * degree});
        }
        {
            var Q0;
            Q0=makeQuery(id+"F35.boolean.opBoolean","SPLIT",FACE,{"disambiguationData":[TD([makeQuery(id+"F35.opExtrude","SWEPT_FACE",FACE,{"disambiguationData":[OSD([sQuery(id+"F28.wireOp",EDGE,"E44")])]})])],"derivedFrom":makeQuery(id+"F27.boolean.opBoolean","COPY",FACE,{"derivedFrom":makeQuery(id+"F27.opExtrude","SWEPT_FACE",FACE,{"disambiguationData":[OSD([sQuery(id+"F26.wireOp",EDGE,"E37")])]})})});
            var sketch = newSketch(context, id + "F31", { "sketchPlane" : qUnion([Q0])});
            skLineSegment(sketch, "E48", {"start": v(-114.27, 0) * mm, "end": v(-114.27, 34.68) * mm});
            skLineSegment(sketch, "E49", {"start": v(-114.27, 34.68) * mm, "end": v(-91.44, 34.68) * mm});
            skLineSegment(sketch, "E50", {"start": v(-91.44, 34.68) * mm, "end": v(-114.27, 0) * mm});
            skSolve(sketch);
        }
        {
            var Q0;
            Q0 = qSketchRegion(id + "F31", true);
            var Q1;
            Q1=sQuery(id+"F5.wireOp",EDGE,"E13");
            revolve(context, id + "F32", {"operationType" : NewBodyOperationType.ADD, "entities" : qUnion([Q0]), "axis" : qUnion([Q1]), "revolveType" : RevolveType.ONE_DIRECTION, "angle" : 6 * degree});
        }
        {
            var Q0;
            {var subQ0=makeQuery(id+"F9.opRevolve","SWEPT_FACE",FACE,{"disambiguationData":[OSD([sQuery(id+"F8.wireOp",EDGE,"E21")])]});var subQ1=makeQuery(id+"F6.opRevolve","SWEPT_FACE",FACE,{"disambiguationData":[OSD([sQuery(id+"F5.wireOp",EDGE,"E16")])]});var subQ4=makeQuery(id+"F15.opRevolve","SWEPT_FACE",FACE,{"disambiguationData":[OSD([sQuery(id+"F14.wireOp",EDGE,"E26")])]});var subQ5=makeQuery(id+"F15.boolean.opBoolean","COPY",FACE,{"disambiguationData":[TD([makeQuery(id+"F7.opPattern","COPY",FACE,{"derivedFrom":subQ1,"instanceName":"1"})])],"derivedFrom":subQ4});var subQ6=makeQuery(id+"F15.boolean.opBoolean","COPY",FACE,{"disambiguationData":[TD([subQ1])],"derivedFrom":subQ4});Q0=makeQuery(id+"F20.opBoolean","MERGE",FACE,{"derivedFrom":[subQ0,subQ6,subQ5,makeQuery(id+"F16.opPattern","COPY",FACE,{"derivedFrom":subQ0,"instanceName":"1"}),makeQuery(id+"F16.opPattern","COPY",FACE,{"derivedFrom":subQ6,"instanceName":"1"}),makeQuery(id+"F16.opPattern","COPY",FACE,{"derivedFrom":subQ5,"instanceName":"1"}),makeQuery(id+"F16.opPattern","COPY",FACE,{"derivedFrom":subQ0,"instanceName":"2"}),makeQuery(id+"F16.opPattern","COPY",FACE,{"derivedFrom":subQ6,"instanceName":"2"}),makeQuery(id+"F16.opPattern","COPY",FACE,{"derivedFrom":subQ5,"instanceName":"2"}),makeQuery(id+"F18.opPattern","COPY",FACE,{"derivedFrom":subQ0,"instanceName":"1"}),makeQuery(id+"F18.opPattern","COPY",FACE,{"derivedFrom":subQ0,"instanceName":"2"})]});}
            var sketch = newSketch(context, id + "F33", { "sketchPlane" : qUnion([Q0])});
            skLineSegment(sketch, "E51", {"start": v(-43.84, -75.93) * mm, "end": v(-47.02, -70.43) * mm});
            skLineSegment(sketch, "E52", {"start": v(-47.02, -70.43) * mm, "end": v(-56.49, -86.84) * mm});
            skLineSegment(sketch, "E53", {"start": v(-56.49, -86.84) * mm, "end": v(-50.14, -86.84) * mm});
            skLineSegment(sketch, "E54", {"start": v(-50.14, -86.84) * mm, "end": v(-43.84, -75.93) * mm});
            skLineSegment(sketch, "E55", {"start": v(-57.13, -98.96) * mm, "end": v(-64.69, -94.6) * mm, "construction": true});
            skSolve(sketch);
        }
        {
            var Q0;
            Q0 = qSketchRegion(id + "F33", true);
            var Q1;
            {var subQ0=makeQuery(id+"F9.opRevolve","SWEPT_FACE",FACE,{"disambiguationData":[OSD([sQuery(id+"F8.wireOp",EDGE,"E22")])]});Q1=makeQuery(id+"F20.opBoolean","MERGE",FACE,{"derivedFrom":[subQ0,makeQuery(id+"F16.opPattern","COPY",FACE,{"derivedFrom":subQ0,"instanceName":"2"}),makeQuery(id+"F18.opPattern","COPY",FACE,{"derivedFrom":subQ0,"instanceName":"1"}),makeQuery(id+"F18.opPattern","COPY",FACE,{"derivedFrom":subQ0,"instanceName":"2"}),makeQuery(id+"F16.opPattern","COPY",FACE,{"derivedFrom":subQ0,"instanceName":"1"})]});}
            extrude(context, id + "F34", {"entities" : qUnion([Q0]), "operationType" : NewBodyOperationType.ADD, "endBound" : BoundingType.UP_TO_SURFACE, "oppositeDirection" : true, "endBoundEntityFace" : qUnion([Q1]), "depth" : 25.4 * mm});
        }
        {
            var Q0;
            Q0 = qSketchRegion(id + "F28", true);
            var Q1;
            {var subQ0=sQuery(id+"F8.wireOp",EDGE,"E22");var subQ1=makeQuery(id+"F9.opRevolve","SWEPT_FACE",FACE,{"disambiguationData":[OSD([subQ0])]});Q1=makeQuery(id+"F34.boolean.opBoolean","MERGE",FACE,{"derivedFrom":[makeQuery(id+"F20.opBoolean","MERGE",FACE,{"derivedFrom":[subQ1,makeQuery(id+"F16.opPattern","COPY",FACE,{"derivedFrom":subQ1,"instanceName":"2"}),makeQuery(id+"F18.opPattern","COPY",FACE,{"derivedFrom":subQ1,"instanceName":"1"}),makeQuery(id+"F18.opPattern","COPY",FACE,{"derivedFrom":subQ1,"instanceName":"2"}),makeQuery(id+"F16.opPattern","COPY",FACE,{"derivedFrom":subQ1,"instanceName":"1"})]}),makeQuery(id+"F34.opExtrude","CAP_FACE",FACE,{"disambiguationData":[OSD([subQ0])],"isStart":false})]});}
            extrude(context, id + "F35", {"entities" : qUnion([Q0]), "operationType" : NewBodyOperationType.REMOVE, "endBound" : BoundingType.UP_TO_SURFACE, "oppositeDirection" : true, "endBoundEntityFace" : qUnion([Q1]), "depth" : 25.4 * mm});
        }
        {
            var Q0;
            Q0=makeQuery(id+"F30.boolean.opBoolean","INTERSECT",EDGE,{"derivedFrom":[makeQuery(id+"F16.opPattern","COPY",FACE,{"derivedFrom":makeQuery(id+"F6.opRevolve","SWEPT_FACE",FACE,{"disambiguationData":[OSD([sQuery(id+"F5.wireOp",EDGE,"E16")])]}),"instanceName":"2"}),makeQuery(id+"F30.opRevolve","SWEPT_FACE",FACE,{"disambiguationData":[OSD([sQuery(id+"F29.wireOp",EDGE,"E47")])]})]});
            var Q1;
            Q1=makeQuery(id+"F32.boolean.opBoolean","INTERSECT",EDGE,{"derivedFrom":[makeQuery(id+"F16.opPattern","COPY",FACE,{"derivedFrom":makeQuery(id+"F7.opPattern","COPY",FACE,{"derivedFrom":makeQuery(id+"F6.opRevolve","SWEPT_FACE",FACE,{"disambiguationData":[OSD([sQuery(id+"F5.wireOp",EDGE,"E16")])]}),"instanceName":"1"}),"instanceName":"1"}),makeQuery(id+"F32.opRevolve","SWEPT_FACE",FACE,{"disambiguationData":[OSD([sQuery(id+"F31.wireOp",EDGE,"E48")])]})]});
            fillet(context, id + "F36", {"entities" : qUnion([Q0, Q1]), "radius" : 25.4 * mm, "tangentPropagation" : true, "allowEdgeOverflow" : false});
        }
        {
            var Q0;
            {var subQ0=makeQuery(id+"F9.opRevolve","SWEPT_EDGE",EDGE,{"disambiguationData":[OSD([sQuery(id+"F8.wireOp",EDGE,"E20"),sQuery(id+"F8.wireOp",EDGE,"E21")])]});Q0=makeQuery(id+"F20.opBoolean","MERGE",EDGE,{"derivedFrom":[subQ0,makeQuery(id+"F16.opPattern","COPY",EDGE,{"derivedFrom":subQ0,"instanceName":"1"}),makeQuery(id+"F16.opPattern","COPY",EDGE,{"derivedFrom":subQ0,"instanceName":"2"}),makeQuery(id+"F18.opPattern","COPY",EDGE,{"derivedFrom":subQ0,"instanceName":"1"}),makeQuery(id+"F18.opPattern","COPY",EDGE,{"derivedFrom":subQ0,"instanceName":"2"})]});}
            chamfer(context, id + "F37", {"entities" : qUnion([Q0]), "width" : 2.54 * mm, "tangentPropagation" : true});
        }
        {
            var Q0;
            Q0=makeQuery(id+"F16.opPattern","COPY",EDGE,{"derivedFrom":makeQuery(id+"F11.boolean.opBoolean","INTERSECT",EDGE,{"derivedFrom":[makeQuery(id+"F6.opRevolve","SWEPT_FACE",FACE,{"disambiguationData":[OSD([sQuery(id+"F5.wireOp",EDGE,"E15")])]}),makeQuery(id+"F11.opExtrude","SWEPT_FACE",FACE,{"disambiguationData":[OSD([sQuery(id+"F10.wireOp",EDGE,"E24")])]})]}),"instanceName":"2"});
            var Q1;
            Q1=makeQuery(id+"F16.opPattern","COPY",EDGE,{"derivedFrom":makeQuery(id+"F13.boolean.opBoolean","INTERSECT",EDGE,{"derivedFrom":[makeQuery(id+"F7.opPattern","COPY",FACE,{"derivedFrom":makeQuery(id+"F6.opRevolve","SWEPT_FACE",FACE,{"disambiguationData":[OSD([sQuery(id+"F5.wireOp",EDGE,"E15")])]}),"instanceName":"1"}),makeQuery(id+"F13.opExtrude","SWEPT_FACE",FACE,{"disambiguationData":[OSD([sQuery(id+"F12.wireOp",EDGE,"E25")])]})]}),"instanceName":"1"});
            fillet(context, id + "F38", {"entities" : qUnion([Q0, Q1]), "radius" : 2.54 * mm, "tangentPropagation" : true, "allowEdgeOverflow" : false});
        }
        {
            var Q0;
            {var subQ0=sQuery(id+"F8.wireOp",EDGE,"E23");var subQ1=sQuery(id+"F8.wireOp",EDGE,"E22");var subQ2=sQuery(id+"F8.wireOp",EDGE,"E21");var subQ3=sQuery(id+"F8.wireOp",EDGE,"E20");var subQ7=makeQuery(id+"F9.opRevolve","SWEPT_EDGE",EDGE,{"disambiguationData":[OSD([subQ1,subQ0])]});var subQ8=makeQuery(id+"F9.opRevolve","CAP_FACE",FACE,{"disambiguationData":[OSD([subQ3,subQ2,subQ1,subQ0])],"isStart":false});var subQ9=makeQuery(id+"F13.boolean.opBoolean","SPLIT",EDGE,{"disambiguationData":[TD([subQ8])],"derivedFrom":makeQuery(id+"F11.boolean.opBoolean","SPLIT",EDGE,{"disambiguationData":[TD([subQ8])],"derivedFrom":subQ7})});Q0=makeQuery(id+"F20.opBoolean","MERGE",EDGE,{"derivedFrom":[makeQuery(id+"F16.opPattern","COPY",EDGE,{"derivedFrom":subQ9,"instanceName":"1"}),makeQuery(id+"F18.opPattern","COPY",EDGE,{"derivedFrom":subQ9,"instanceName":"1"}),makeQuery(id+"F18.opPattern","COPY",EDGE,{"derivedFrom":makeQuery(id+"F11.boolean.opBoolean","SPLIT",EDGE,{"disambiguationData":[TD([makeQuery(id+"F9.opRevolve","CAP_FACE",FACE,{"disambiguationData":[OSD([subQ3,subQ2,subQ1,subQ0])],"isStart":true})])],"derivedFrom":subQ7}),"instanceName":"2"})]});}
            var Q1;
            {var subQ0=makeQuery(id+"F9.opRevolve","SWEPT_EDGE",EDGE,{"disambiguationData":[OSD([sQuery(id+"F8.wireOp",EDGE,"E20"),sQuery(id+"F8.wireOp",EDGE,"E22")])]});Q1=makeQuery(id+"F20.opBoolean","MERGE",EDGE,{"derivedFrom":[subQ0,makeQuery(id+"F16.opPattern","COPY",EDGE,{"derivedFrom":subQ0,"instanceName":"1"}),makeQuery(id+"F16.opPattern","COPY",EDGE,{"derivedFrom":subQ0,"instanceName":"2"}),makeQuery(id+"F18.opPattern","COPY",EDGE,{"derivedFrom":subQ0,"instanceName":"1"}),makeQuery(id+"F18.opPattern","COPY",EDGE,{"derivedFrom":subQ0,"instanceName":"2"})]});}
            fillet(context, id + "F39", {"entities" : qUnion([Q0, Q1]), "radius" : 2.54 * mm, "tangentPropagation" : true, "allowEdgeOverflow" : false});
        }
        {
            var Q0;
            {var subQ0=makeQuery(id+"F9.opRevolve","SWEPT_FACE",FACE,{"disambiguationData":[OSD([sQuery(id+"F8.wireOp",EDGE,"E21")])]});var subQ1=subQ0;var subQ2=makeQuery(id+"F16.opPattern","COPY",FACE,{"derivedFrom":subQ1,"instanceName":"2"});var subQ3=makeQuery(id+"F6.opRevolve","SWEPT_FACE",FACE,{"disambiguationData":[OSD([sQuery(id+"F5.wireOp",EDGE,"E16")])]});var subQ6=makeQuery(id+"F15.opRevolve","SWEPT_FACE",FACE,{"disambiguationData":[OSD([sQuery(id+"F14.wireOp",EDGE,"E26")])]});var subQ7=makeQuery(id+"F15.boolean.opBoolean","COPY",FACE,{"disambiguationData":[TD([subQ3])],"derivedFrom":subQ6});var subQ8=makeQuery(id+"F16.opPattern","COPY",FACE,{"derivedFrom":subQ7,"instanceName":"1"});var subQ9=makeQuery(id+"F15.boolean.opBoolean","COPY",FACE,{"disambiguationData":[TD([makeQuery(id+"F7.opPattern","COPY",FACE,{"derivedFrom":subQ3,"instanceName":"1"})])],"derivedFrom":subQ6});var subQ10=makeQuery(id+"F16.opPattern","COPY",FACE,{"derivedFrom":subQ9,"instanceName":"1"});var subQ12=makeQuery(id+"F16.opPattern","COPY",FACE,{"derivedFrom":subQ1,"instanceName":"1"});var subQ13=makeQuery(id+"F9.opRevolve","SWEPT_FACE",FACE,{"disambiguationData":[OSD([sQuery(id+"F8.wireOp",EDGE,"E20")])]});var subQ14=makeQuery(id+"F16.opPattern","COPY",FACE,{"derivedFrom":subQ7,"instanceName":"2"});var subQ15=makeQuery(id+"F16.opPattern","COPY",FACE,{"derivedFrom":subQ9,"instanceName":"2"});var subQ16=makeQuery(id+"F18.opPattern","COPY",FACE,{"derivedFrom":subQ1,"instanceName":"1"});var subQ17=makeQuery(id+"F18.opPattern","COPY",FACE,{"derivedFrom":subQ1,"instanceName":"2"});var subQ18=sQuery(id+"F29.wireOp",EDGE,"E46");var subQ19=makeQuery(id+"F27.opExtrude","SWEPT_FACE",FACE,{"disambiguationData":[OSD([sQuery(id+"F26.wireOp",EDGE,"E38")])]});Q0=makeQuery(id+"F34.boolean.opBoolean","SPLIT",EDGE,{"disambiguationData":[TD([subQ13])],"derivedFrom":makeQuery(id+"F30.boolean.opBoolean","MERGE",EDGE,{"derivedFrom":[makeQuery(id+"F27.boolean.opBoolean","INTERSECT",EDGE,{"derivedFrom":[makeQuery(id+"F20.opBoolean","MERGE",FACE,{"derivedFrom":[subQ1,subQ7,subQ9,subQ12,subQ8,subQ10,subQ2,subQ14,subQ15,subQ16,subQ17]}),subQ19]}),makeQuery(id+"F30.opRevolve","CAP_EDGE",EDGE,{"disambiguationData":[OSD([subQ18])],"isStart":true})]})});}
            var Q1;
            {var subQ0=makeQuery(id+"F6.opRevolve","SWEPT_FACE",FACE,{"disambiguationData":[OSD([sQuery(id+"F5.wireOp",EDGE,"E16")])]});var subQ3=makeQuery(id+"F15.opRevolve","SWEPT_FACE",FACE,{"disambiguationData":[OSD([sQuery(id+"F14.wireOp",EDGE,"E26")])]});var subQ4=makeQuery(id+"F15.boolean.opBoolean","COPY",FACE,{"disambiguationData":[TD([makeQuery(id+"F7.opPattern","COPY",FACE,{"derivedFrom":subQ0,"instanceName":"1"})])],"derivedFrom":subQ3});var subQ5=makeQuery(id+"F16.opPattern","COPY",FACE,{"derivedFrom":subQ4,"instanceName":"2"});var subQ7=makeQuery(id+"F15.boolean.opBoolean","COPY",FACE,{"disambiguationData":[TD([subQ0])],"derivedFrom":subQ3});var subQ8=makeQuery(id+"F16.opPattern","COPY",FACE,{"derivedFrom":subQ7,"instanceName":"2"});var subQ9=makeQuery(id+"F9.opRevolve","SWEPT_FACE",FACE,{"disambiguationData":[OSD([sQuery(id+"F8.wireOp",EDGE,"E21")])]});var subQ10=subQ9;var subQ11=makeQuery(id+"F18.opPattern","COPY",FACE,{"derivedFrom":subQ10,"instanceName":"1"});var subQ12=makeQuery(id+"F16.opPattern","COPY",FACE,{"derivedFrom":subQ10,"instanceName":"2"});var subQ13=makeQuery(id+"F16.opPattern","COPY",FACE,{"derivedFrom":subQ7,"instanceName":"1"});var subQ14=makeQuery(id+"F16.opPattern","COPY",FACE,{"derivedFrom":subQ4,"instanceName":"1"});var subQ15=makeQuery(id+"F16.opPattern","COPY",FACE,{"derivedFrom":subQ10,"instanceName":"1"});var subQ16=makeQuery(id+"F18.opPattern","COPY",FACE,{"derivedFrom":subQ10,"instanceName":"2"});var subQ17=sQuery(id+"F29.wireOp",EDGE,"E46");var subQ18=makeQuery(id+"F27.opExtrude","SWEPT_FACE",FACE,{"disambiguationData":[OSD([sQuery(id+"F26.wireOp",EDGE,"E38")])]});var subQ19=sQuery(id+"F29.wireOp",EDGE,"E47");Q1=makeQuery(id+"F34.boolean.opBoolean","SPLIT",EDGE,{"disambiguationData":[TD([makeQuery(id+"F30.opRevolve","SWEPT_FACE",FACE,{"disambiguationData":[OSD([subQ19])]})])],"derivedFrom":makeQuery(id+"F30.boolean.opBoolean","MERGE",EDGE,{"derivedFrom":[makeQuery(id+"F27.boolean.opBoolean","INTERSECT",EDGE,{"derivedFrom":[makeQuery(id+"F20.opBoolean","MERGE",FACE,{"derivedFrom":[subQ10,subQ7,subQ4,subQ15,subQ13,subQ14,subQ12,subQ8,subQ5,subQ11,subQ16]}),subQ18]}),makeQuery(id+"F30.opRevolve","CAP_EDGE",EDGE,{"disambiguationData":[OSD([subQ17])],"isStart":true})]})});}
            chamfer(context, id + "F40", {"entities" : qUnion([Q0, Q1]), "width" : 2.54 * mm, "tangentPropagation" : true});
        }
        {
            var Q0;
            {var subQ0=makeQuery(id+"F9.opRevolve","SWEPT_FACE",FACE,{"disambiguationData":[OSD([sQuery(id+"F8.wireOp",EDGE,"E21")])]});var subQ1=subQ0;var subQ2=makeQuery(id+"F16.opPattern","COPY",FACE,{"derivedFrom":subQ1,"instanceName":"2"});var subQ3=makeQuery(id+"F6.opRevolve","SWEPT_FACE",FACE,{"disambiguationData":[OSD([sQuery(id+"F5.wireOp",EDGE,"E16")])]});var subQ6=makeQuery(id+"F15.opRevolve","SWEPT_FACE",FACE,{"disambiguationData":[OSD([sQuery(id+"F14.wireOp",EDGE,"E26")])]});var subQ7=makeQuery(id+"F15.boolean.opBoolean","COPY",FACE,{"disambiguationData":[TD([subQ3])],"derivedFrom":subQ6});var subQ8=makeQuery(id+"F16.opPattern","COPY",FACE,{"derivedFrom":subQ7,"instanceName":"1"});var subQ9=makeQuery(id+"F15.boolean.opBoolean","COPY",FACE,{"disambiguationData":[TD([makeQuery(id+"F7.opPattern","COPY",FACE,{"derivedFrom":subQ3,"instanceName":"1"})])],"derivedFrom":subQ6});var subQ10=makeQuery(id+"F16.opPattern","COPY",FACE,{"derivedFrom":subQ9,"instanceName":"1"});var subQ11=makeQuery(id+"F16.opPattern","COPY",FACE,{"derivedFrom":subQ1,"instanceName":"1"});var subQ12=makeQuery(id+"F9.opRevolve","SWEPT_FACE",FACE,{"disambiguationData":[OSD([sQuery(id+"F8.wireOp",EDGE,"E20")])]});var subQ13=sQuery(id+"F31.wireOp",EDGE,"E49");var subQ14=makeQuery(id+"F16.opPattern","COPY",FACE,{"derivedFrom":subQ7,"instanceName":"2"});var subQ15=makeQuery(id+"F16.opPattern","COPY",FACE,{"derivedFrom":subQ9,"instanceName":"2"});var subQ16=makeQuery(id+"F18.opPattern","COPY",FACE,{"derivedFrom":subQ1,"instanceName":"1"});var subQ17=makeQuery(id+"F18.opPattern","COPY",FACE,{"derivedFrom":subQ1,"instanceName":"2"});var subQ18=makeQuery(id+"F27.opExtrude","SWEPT_FACE",FACE,{"disambiguationData":[OSD([sQuery(id+"F26.wireOp",EDGE,"E37")])]});Q0=makeQuery(id+"F35.boolean.opBoolean","SPLIT",EDGE,{"disambiguationData":[TD([subQ12])],"derivedFrom":makeQuery(id+"F32.boolean.opBoolean","MERGE",EDGE,{"derivedFrom":[makeQuery(id+"F27.boolean.opBoolean","INTERSECT",EDGE,{"derivedFrom":[makeQuery(id+"F20.opBoolean","MERGE",FACE,{"derivedFrom":[subQ1,subQ7,subQ9,subQ11,subQ8,subQ10,subQ2,subQ14,subQ15,subQ16,subQ17]}),subQ18]}),makeQuery(id+"F32.opRevolve","CAP_EDGE",EDGE,{"disambiguationData":[OSD([subQ13])],"isStart":true})]})});}
            var Q1;
            Q1=makeQuery(id+"F35.boolean.opBoolean","COPY",EDGE,{"derivedFrom":makeQuery(id+"F35.opExtrude","CAP_EDGE",EDGE,{"disambiguationData":[OSD([sQuery(id+"F28.wireOp",EDGE,"E44")])],"isStart":true})});
            var Q2;
            {var subQ0=makeQuery(id+"F6.opRevolve","SWEPT_FACE",FACE,{"disambiguationData":[OSD([sQuery(id+"F5.wireOp",EDGE,"E16")])]});var subQ3=makeQuery(id+"F15.opRevolve","SWEPT_FACE",FACE,{"disambiguationData":[OSD([sQuery(id+"F14.wireOp",EDGE,"E26")])]});var subQ4=makeQuery(id+"F15.boolean.opBoolean","COPY",FACE,{"disambiguationData":[TD([makeQuery(id+"F7.opPattern","COPY",FACE,{"derivedFrom":subQ0,"instanceName":"1"})])],"derivedFrom":subQ3});var subQ5=makeQuery(id+"F16.opPattern","COPY",FACE,{"derivedFrom":subQ4,"instanceName":"2"});var subQ6=makeQuery(id+"F15.boolean.opBoolean","COPY",FACE,{"disambiguationData":[TD([subQ0])],"derivedFrom":subQ3});var subQ7=makeQuery(id+"F16.opPattern","COPY",FACE,{"derivedFrom":subQ6,"instanceName":"2"});var subQ8=makeQuery(id+"F9.opRevolve","SWEPT_FACE",FACE,{"disambiguationData":[OSD([sQuery(id+"F8.wireOp",EDGE,"E21")])]});var subQ9=subQ8;var subQ10=makeQuery(id+"F18.opPattern","COPY",FACE,{"derivedFrom":subQ9,"instanceName":"1"});var subQ11=makeQuery(id+"F16.opPattern","COPY",FACE,{"derivedFrom":subQ9,"instanceName":"2"});var subQ12=makeQuery(id+"F16.opPattern","COPY",FACE,{"derivedFrom":subQ6,"instanceName":"1"});var subQ13=makeQuery(id+"F16.opPattern","COPY",FACE,{"derivedFrom":subQ4,"instanceName":"1"});var subQ14=makeQuery(id+"F16.opPattern","COPY",FACE,{"derivedFrom":subQ9,"instanceName":"1"});var subQ15=sQuery(id+"F31.wireOp",EDGE,"E49");var subQ16=makeQuery(id+"F18.opPattern","COPY",FACE,{"derivedFrom":subQ9,"instanceName":"2"});var subQ17=makeQuery(id+"F27.opExtrude","SWEPT_FACE",FACE,{"disambiguationData":[OSD([sQuery(id+"F26.wireOp",EDGE,"E37")])]});var subQ18=sQuery(id+"F31.wireOp",EDGE,"E48");Q2=makeQuery(id+"F35.boolean.opBoolean","SPLIT",EDGE,{"disambiguationData":[TD([makeQuery(id+"F32.opRevolve","SWEPT_FACE",FACE,{"disambiguationData":[OSD([subQ18])]})])],"derivedFrom":makeQuery(id+"F32.boolean.opBoolean","MERGE",EDGE,{"derivedFrom":[makeQuery(id+"F27.boolean.opBoolean","INTERSECT",EDGE,{"derivedFrom":[makeQuery(id+"F20.opBoolean","MERGE",FACE,{"derivedFrom":[subQ9,subQ6,subQ4,subQ14,subQ12,subQ13,subQ11,subQ7,subQ5,subQ10,subQ16]}),subQ17]}),makeQuery(id+"F32.opRevolve","CAP_EDGE",EDGE,{"disambiguationData":[OSD([subQ15])],"isStart":true})]})});}
            var Q3;
            Q3=makeQuery(id+"F35.boolean.opBoolean","COPY",EDGE,{"derivedFrom":makeQuery(id+"F35.opExtrude","CAP_EDGE",EDGE,{"disambiguationData":[OSD([sQuery(id+"F28.wireOp",EDGE,"E43")])],"isStart":true})});
            var Q4;
            Q4=makeQuery(id+"F35.boolean.opBoolean","COPY",EDGE,{"derivedFrom":makeQuery(id+"F35.opExtrude","CAP_EDGE",EDGE,{"disambiguationData":[OSD([sQuery(id+"F28.wireOp",EDGE,"E42")])],"isStart":true})});
            chamfer(context, id + "F41", {"entities" : qUnion([Q0, Q1, Q2, Q3, Q4]), "width" : 2.54 * mm, "tangentPropagation" : true});
        }
        {
            var Q0;
            {var subQ0=makeQuery(id+"F9.opRevolve","SWEPT_FACE",FACE,{"disambiguationData":[OSD([sQuery(id+"F8.wireOp",EDGE,"E22")])]});Q0=makeQuery(id+"F20.opBoolean","INTERSECT",EDGE,{"derivedFrom":[subQ0,makeQuery(id+"F16.opPattern","COPY",FACE,{"derivedFrom":makeQuery(id+"F7.opPattern","COPY",FACE,{"derivedFrom":makeQuery(id+"F6.opRevolve","SWEPT_FACE",FACE,{"disambiguationData":[OSD([sQuery(id+"F5.wireOp",EDGE,"E16")])]}),"instanceName":"1"}),"instanceName":"1"}),makeQuery(id+"F16.opPattern","COPY",FACE,{"derivedFrom":subQ0,"instanceName":"2"}),makeQuery(id+"F18.opPattern","COPY",FACE,{"derivedFrom":subQ0,"instanceName":"1"}),makeQuery(id+"F18.opPattern","COPY",FACE,{"derivedFrom":subQ0,"instanceName":"2"}),makeQuery(id+"F16.opPattern","COPY",FACE,{"derivedFrom":subQ0,"instanceName":"1"})]});}
            fillet(context, id + "F42", {"entities" : qUnion([Q0]), "radius" : 5.08 * mm, "tangentPropagation" : true, "allowEdgeOverflow" : false});
        }
        {
            var Q0;
            {var subQ0=makeQuery(id+"F9.opRevolve","SWEPT_FACE",FACE,{"disambiguationData":[OSD([sQuery(id+"F8.wireOp",EDGE,"E22")])]});Q0=makeQuery(id+"F20.opBoolean","INTERSECT",EDGE,{"derivedFrom":[makeQuery(id+"F16.opPattern","COPY",FACE,{"derivedFrom":subQ0,"instanceName":"2"}),makeQuery(id+"F16.opPattern","COPY",FACE,{"derivedFrom":makeQuery(id+"F6.opRevolve","SWEPT_FACE",FACE,{"disambiguationData":[OSD([sQuery(id+"F5.wireOp",EDGE,"E16")])]}),"instanceName":"2"}),makeQuery(id+"F18.opPattern","COPY",FACE,{"derivedFrom":subQ0,"instanceName":"2"})]});}
            fillet(context, id + "F43", {"entities" : qUnion([Q0]), "radius" : 5.08 * mm, "tangentPropagation" : true, "allowEdgeOverflow" : false});
        }
        {
            var Q0;
            Q0=makeQuery(id+"F25.boolean.opBoolean","COPY",FACE,{"derivedFrom":makeQuery(id+"F25.opPattern","COPY",FACE,{"derivedFrom":makeQuery(id+"F24.opExtrude","SWEPT_FACE",FACE,{"disambiguationData":[OSD([sQuery(id+"F23.wireOp",EDGE,"E36")])]}),"instanceName":"2"})});
            var Q1;
            Q1=makeQuery(id+"F25.boolean.opBoolean","COPY",FACE,{"derivedFrom":makeQuery(id+"F25.opPattern","COPY",FACE,{"derivedFrom":makeQuery(id+"F24.opExtrude","CAP_FACE",FACE,{"disambiguationData":[OSD([sQuery(id+"F23.wireOp",EDGE,"E36")])],"isStart":true}),"instanceName":"2"})});
            fillet(context, id + "F44", {"entities" : qUnion([Q0, Q1]), "radius" : 2.03 * mm, "tangentPropagation" : true, "allowEdgeOverflow" : false});
        }
    });
